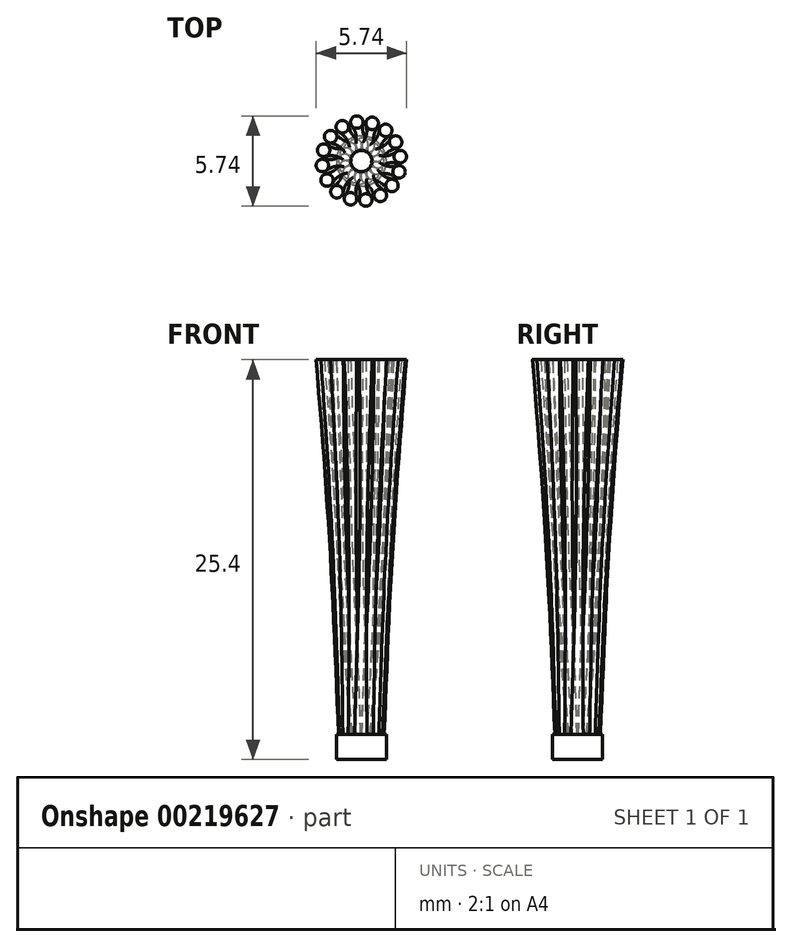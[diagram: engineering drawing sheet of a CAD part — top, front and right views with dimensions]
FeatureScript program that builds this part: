
annotation { "Feature Type Name" : "Feature", "Feature Type Description" : "" }
export const myFeature = defineFeature(function(context is Context, id is Id, definition is map)
    precondition{}
    {
        {
            var Q0;
            Q0=qCreatedBy(makeId("Top.planeOp"),FACE);
            var sketch = newSketch(context, id + "F0", { "sketchPlane" : qUnion([Q0])});
            skCircle(sketch, "E0", {"center": v(0, 0) * mm, "radius": 1.59 * mm});
            skSolve(sketch);
        }
        {
            var Q0;
            Q0=qCreatedBy(makeId("Top.planeOp"),FACE);
            cPlane(context, id + "F1", {"entities" : qUnion([Q0]), "cplaneType" : CPlaneType.OFFSET, "offset" : 25.4 * mm, "width" : 152.4 * mm, "height" : 152.4 * mm});
        }
        {
            var Q0;
            Q0=qCreatedBy(id+"F1.planeOp",FACE);
            var sketch = newSketch(context, id + "F2", { "sketchPlane" : qUnion([Q0])});
            skCircle(sketch, "E1", {"center": v(-1.55, -1.95) * mm, "radius": 0.4 * mm});
            skSolve(sketch);
        }
        {
            var Q0;
            Q0 = qSketchRegion(id + "F0", true);
            extrude(context, id + "F3", {"entities" : qUnion([Q0]), "depth" : 1.59 * mm});
        }
        {
            var Q0;
            Q0=makeQuery(id+"F3.opExtrude","CAP_FACE",FACE,{"disambiguationData":[OSD([sQuery(id+"F0.wireOp",EDGE,"E0")])],"isStart":false});
            var sketch = newSketch(context, id + "F4", { "sketchPlane" : qUnion([Q0])});
            skCircle(sketch, "E2", {"center": v(-0.77, -0.72) * mm, "radius": 0.4 * mm});
            skSolve(sketch);
        }
        {
            var Q1;
            Q1=makeQuery(id+"F2.imprint","IMPRINT",FACE,{"disambiguationData":[TD([[makeQuery(id+"F2.imprint","IMPRINT",EDGE,{"derivedFrom":sQuery(id+"F2.wireOp",EDGE,"E1")}),1.0]])]});
            var Q2;
            Q2=makeQuery(id+"F4.imprint","IMPRINT",FACE,{"disambiguationData":[TD([[makeQuery(id+"F4.imprint","IMPRINT",EDGE,{"derivedFrom":sQuery(id+"F4.wireOp",EDGE,"E2")}),1.0]])]});
            loft(context, id + "F5", {"sheetProfilesArray" : [{ "sheetProfileEntities" : qUnion([Q1]) }, { "sheetProfileEntities" : qUnion([Q2]) }]});
        }
        {
            var Q0;
            Q0=makeQuery(id+"F5.opLoft","SWEPT_BODY",BODY,{"disambiguationData":[OSD([makeQuery(id+"F2.imprint","IMPRINT",FACE,{"disambiguationData":[TD([[makeQuery(id+"F2.imprint","IMPRINT",EDGE,{"derivedFrom":sQuery(id+"F2.wireOp",EDGE,"E1")}),1.0]])]}),makeQuery(id+"F4.imprint","IMPRINT",FACE,{"disambiguationData":[TD([[makeQuery(id+"F4.imprint","IMPRINT",EDGE,{"derivedFrom":sQuery(id+"F4.wireOp",EDGE,"E2")}),1.0]])]})])]});
            var Q1;
            Q1=sQuery(id+"F0.wireOp",EDGE,"E0");
            circularPattern(context, id + "F6", {"entities" : qUnion([Q0]), "axis" : qUnion([Q1]), "angle" : 360 * degree, "instanceCount" : 16, "equalSpace" : true});
        }
    });
